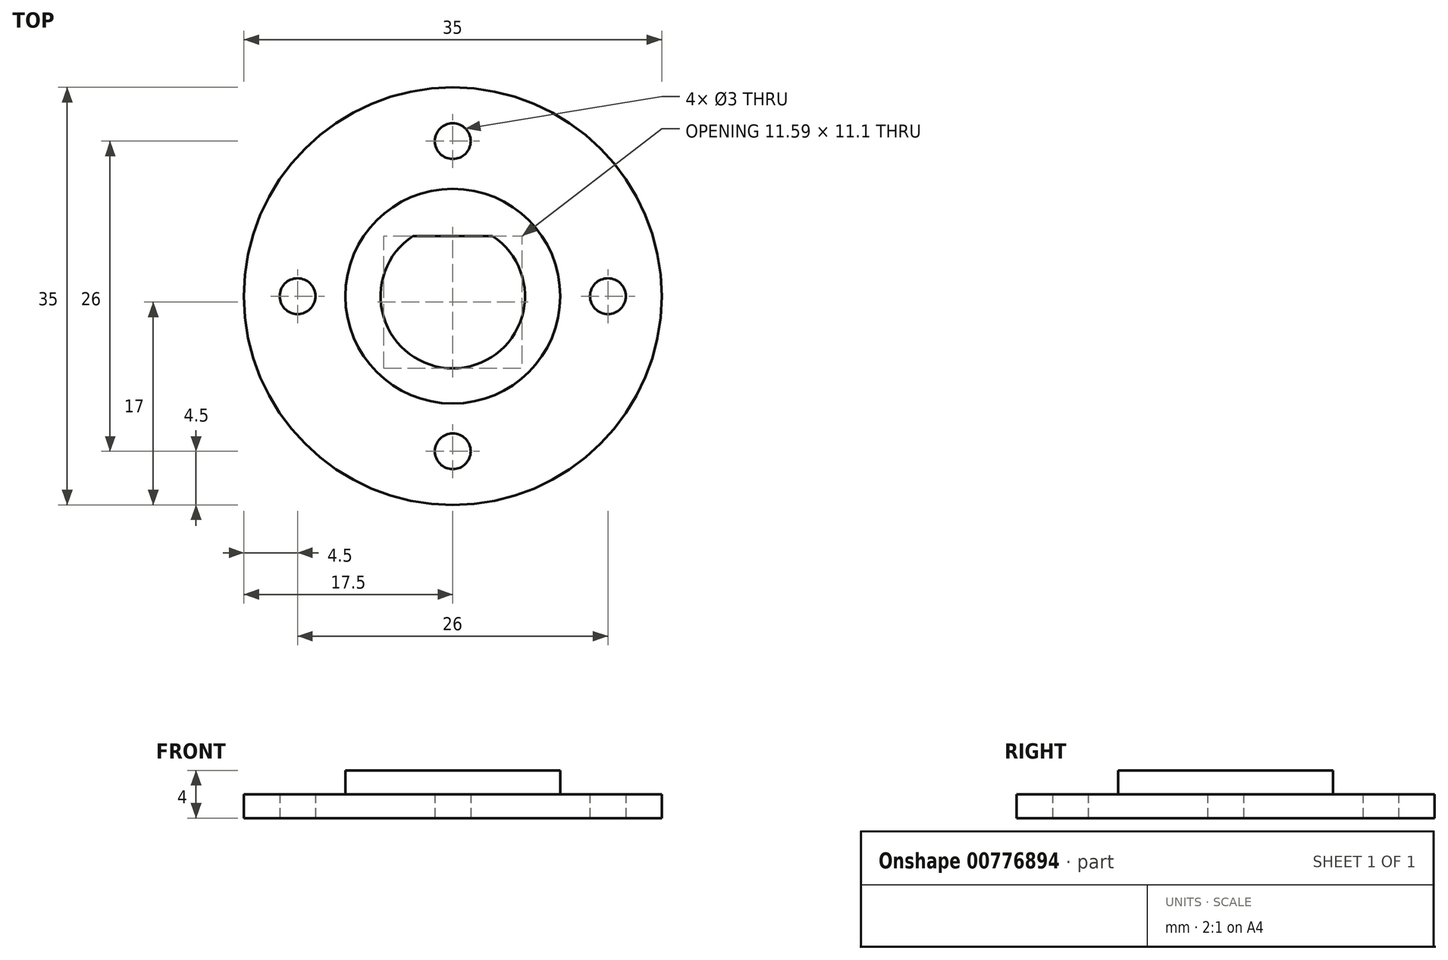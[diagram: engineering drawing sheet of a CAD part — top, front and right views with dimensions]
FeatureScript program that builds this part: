
annotation { "Feature Type Name" : "Feature", "Feature Type Description" : "" }
export const myFeature = defineFeature(function(context is Context, id is Id, definition is map)
    precondition{}
    {
        {
            var Q0;
            Q0=qCreatedBy(makeId("Top.planeOp"),FACE);
            var sketch = newSketch(context, id + "F0", { "sketchPlane" : qUnion([Q0])});
            skArc(sketch, "E0", {"start": v(-3.33, 5.05) * mm, "mid": v(0, -6.05) * mm, "end": v(3.33, 5.05) * mm});
            skLineSegment(sketch, "E1", {"start": v(-3.33, 5.05) * mm, "end": v(3.33, 5.05) * mm});
            skCircle(sketch, "E2", {"center": v(0, 0) * mm, "radius": 17.5 * mm});
            skCircle(sketch, "E3", {"center": v(0, 0) * mm, "radius": 9 * mm});
            skCircle(sketch, "E4", {"center": v(0, 13) * mm, "radius": 1.5 * mm});
            skCircle(sketch, "E5.1.0", {"center": v(-13, 0) * mm, "radius": 1.5 * mm});
            skCircle(sketch, "E5.2.0", {"center": v(0, -13) * mm, "radius": 1.5 * mm});
            skCircle(sketch, "E5.3.0", {"center": v(13, 0) * mm, "radius": 1.5 * mm});
            skSolve(sketch);
        }
        {
            var Q0;
            Q0=makeQuery(id+"F0.imprint","IMPRINT",FACE,{"disambiguationData":[TD([[makeQuery(id+"F0.imprint","IMPRINT",EDGE,{"derivedFrom":sQuery(id+"F0.wireOp",EDGE,"E0")}),-1.0]])]});
            extrude(context, id + "F1", {"entities" : qUnion([Q0]), "depth" : 4 * mm, "offsetDistance" : 25 * mm});
        }
        {
            var Q0;
            Q0=makeQuery(id+"F0.imprint","IMPRINT",FACE,{"disambiguationData":[TD([[makeQuery(id+"F0.imprint","IMPRINT",EDGE,{"derivedFrom":sQuery(id+"F0.wireOp",EDGE,"E2")}),1.0]])]});
            extrude(context, id + "F2", {"entities" : qUnion([Q0]), "operationType" : NewBodyOperationType.ADD, "depth" : 2 * mm, "offsetDistance" : 25 * mm});
        }
    });
